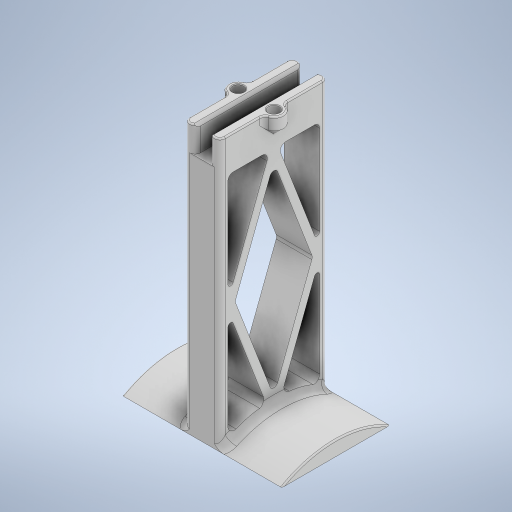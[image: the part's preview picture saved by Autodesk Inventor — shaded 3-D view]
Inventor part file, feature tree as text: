
AUTODESK INVENTOR PART (.ipt)
format: ipt  version: 2024.2 (Build 282272000, 272)  size: 543,744 bytes
history: native  units: mm
features: extrude x6, fillet x4, chamfer x3, plane x1, mirror x1, sketch x1
ambient origin geometry x8: Origin, YZ Plane, XZ Plane, XY Plane, X Axis, Y Axis, Z Axis, Center Point
bodies: Solid1 (feature_tree)
feature tree (16):
  extrude  "Extrusion1"  Depth=1.0mm
  extrude  "Extrusion2"  Depth=13.2mm TaperAngle=0.0deg
  plane  "Work Plane1"
  mirror  "Mirror1"
  extrude  "Extrusion3"  Depth=1.0mm TaperAngle=0.0deg
  extrude  "Extrusion4"  [1 undecoded]
  extrude  "Extrusion5"  Depth=1.0mm
  extrude  "Extrusion7"  Depth=1.0mm
  chamfer  "Chamfer2"  Distance=9.6mm
  fillet  "Fillet1"  Radius=2.0mm
  chamfer  "Chamfer1"  Distance=1.0mm Angle=45.0deg
  fillet  "Fillet2"  Radius=4.1mm
  fillet  "Fillet3"  Radius=7.0mm
  chamfer  "Chamfer3"  Distance=8.0mm
  fillet  "Fillet5"  Radius=3.1mm
  sketch  "Sketch6"  dims[d0=100.0mm d1=40.0mm d2=13.2mm d3=0.0mm d5=23.0mm d6=0.0mm d7=-6.6mm d8=5.2mm d9=4.0mm d10=9.6mm d11=0.0mm d12=2.0mm d13=1.0mm d14=2.0mm d15=45.0deg d16=4.1mm d17=7.0mm d18=8.0mm d19=0.0mm d20=3.1mm d21=0.0mm d22=3.5mm d23=2.0mm d24=45.0deg d25=2.0mm d26=0.5mm d27=0.25mm d28=2.0mm d29=45.0deg d30=40.0mm d41=3.0mm d42=3.0mm d43=3.0mm d44=3.0mm d46=40.5mm d47=3.0mm d48=3.0mm d49=3.0mm d50=35.0mm d51=3.0mm d52=0.8mm d53=10.0mm d54=0.0mm d55=2.0mm d56=1.5mm d57=1.0mm d58=3.0mm d39=0.872665mm d40=0.872665mm]
note: 1 required parameter value undecoded (feature->parameter linkage not recoverable at this tier; creation-order binding heuristic only, values carry confidence <= 0.55)
